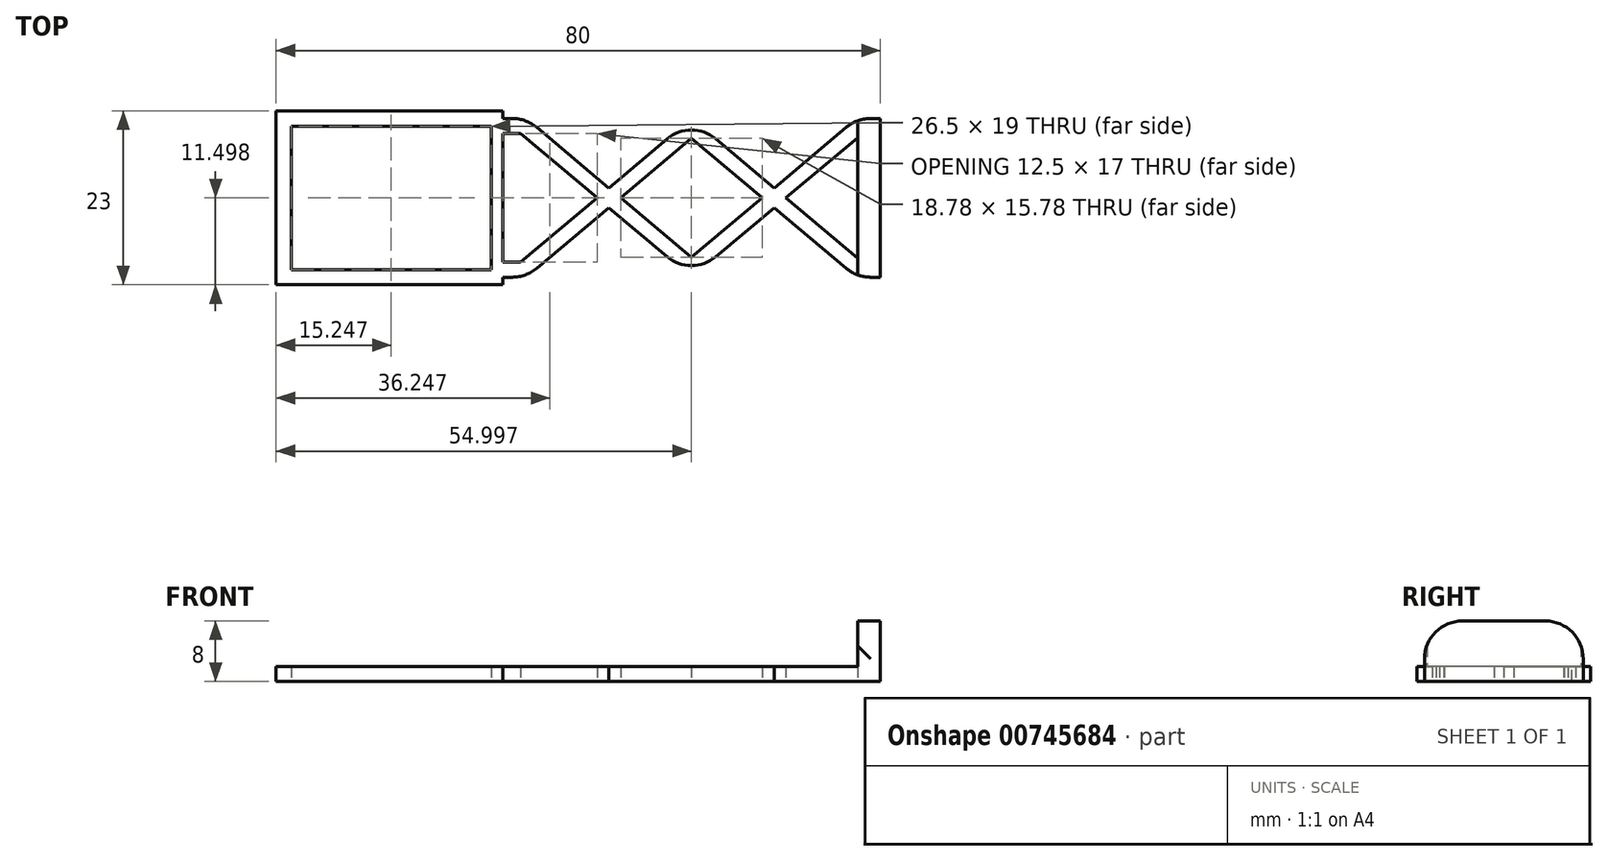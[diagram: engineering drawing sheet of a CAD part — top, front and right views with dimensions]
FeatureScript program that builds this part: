
annotation { "Feature Type Name" : "Feature", "Feature Type Description" : "" }
export const myFeature = defineFeature(function(context is Context, id is Id, definition is map)
    precondition{}
    {
        {
            var Q0;
            Q0=qCreatedBy(makeId("Top.planeOp"),FACE);
            var sketch = newSketch(context, id + "F0", { "sketchPlane" : qUnion([Q0])});
            skLineSegment(sketch, "E0.bottom", {"start": v(-35.23, 8.03) * mm, "end": v(-5.23, 8.03) * mm});
            skLineSegment(sketch, "E0.top", {"start": v(-35.23, -14.97) * mm, "end": v(-5.23, -14.97) * mm});
            skLineSegment(sketch, "E0.left", {"start": v(-35.23, 8.03) * mm, "end": v(-35.23, -14.97) * mm});
            skLineSegment(sketch, "E1.right", {"start": v(44.77, 7.03) * mm, "end": v(44.77, -13.97) * mm});
            skLineSegment(sketch, "E2", {"start": v(-5.23, 8.03) * mm, "end": v(-5.23, 7.03) * mm});
            skLineSegment(sketch, "E3", {"start": v(-5.23, -14.97) * mm, "end": v(-5.23, -13.97) * mm});
            skLineSegment(sketch, "E4.bottom", {"start": v(-33.23, 6.03) * mm, "end": v(-6.73, 6.03) * mm});
            skLineSegment(sketch, "E4.top", {"start": v(-33.23, -12.97) * mm, "end": v(-6.73, -12.97) * mm});
            skLineSegment(sketch, "E4.left", {"start": v(-33.23, 6.03) * mm, "end": v(-33.23, -12.97) * mm});
            skLineSegment(sketch, "E4.right", {"start": v(-6.73, 6.03) * mm, "end": v(-6.73, -12.97) * mm});
            skLineSegment(sketch, "E5", {"start": v(41.77, 7.03) * mm, "end": v(41.77, -13.97) * mm});
            skLineSegment(sketch, "E6", {"start": v(-5.23, 7.03) * mm, "end": v(-5.23, -13.97) * mm});
            skLineSegment(sketch, "E7", {"start": v(-5.23, 7.03) * mm, "end": v(44.77, 7.03) * mm});
            skLineSegment(sketch, "E8", {"start": v(-5.23, -13.97) * mm, "end": v(44.77, -13.97) * mm});
            skLineSegment(sketch, "E9", {"start": v(19.77, 7.03) * mm, "end": v(-5.23, -13.97) * mm});
            skLineSegment(sketch, "E10", {"start": v(19.77, 7.03) * mm, "end": v(44.77, -13.97) * mm});
            skLineSegment(sketch, "E11", {"start": v(-5.23, 7.03) * mm, "end": v(19.77, -13.97) * mm});
            skLineSegment(sketch, "E12", {"start": v(19.77, -13.97) * mm, "end": v(44.77, 7.03) * mm});
            skLineSegment(sketch, "E13", {"start": v(8.82, -4.78) * mm, "end": v(-2.12, -13.97) * mm});
            skLineSegment(sketch, "E14", {"start": v(8.82, -2.17) * mm, "end": v(-2.12, 7.03) * mm});
            skLineSegment(sketch, "E15", {"start": v(8.82, -4.78) * mm, "end": v(21.32, 5.72) * mm});
            skLineSegment(sketch, "E16", {"start": v(8.82, -2.17) * mm, "end": v(21.32, -12.67) * mm});
            skLineSegment(sketch, "E17", {"start": v(30.71, -4.78) * mm, "end": v(41.66, -13.97) * mm});
            skLineSegment(sketch, "E18", {"start": v(30.71, -2.17) * mm, "end": v(41.66, 7.03) * mm});
            skLineSegment(sketch, "E19", {"start": v(30.71, -2.17) * mm, "end": v(19.77, -11.36) * mm});
            skLineSegment(sketch, "E20", {"start": v(30.71, -4.78) * mm, "end": v(19.77, 4.42) * mm});
            skLineSegment(sketch, "E21", {"start": v(-5.23, 5.03) * mm, "end": v(0.26, 5.03) * mm});
            skLineSegment(sketch, "E22", {"start": v(-5.23, -11.97) * mm, "end": v(0.26, -11.97) * mm});
            skSolve(sketch);
        }
        {
            var Q0;
            Q0=makeQuery(id+"F0.imprint","IMPRINT",FACE,{"disambiguationData":[TD([[makeQuery(id+"F0.imprint","IMPRINT",EDGE,{"derivedFrom":sQuery(id+"F0.wireOp",EDGE,"E0.bottom")}),-1.0]])]});
            var Q1;
            {var subQ1=sQuery(id+"F0.wireOp",EDGE,"E6");var subQ3=sQuery(id+"F0.wireOp",EDGE,"E21");var subQ4=makeQuery(id+"F0.imprint","INTERSECT",VERTEX,{"derivedFrom":[subQ1,subQ3]});Q1=makeQuery(id+"F0.imprint","IMPRINT",FACE,{"disambiguationData":[TD([[makeQuery(id+"F0.imprint","IMPRINT",EDGE,{"disambiguationData":[TD([[subQ4,-1.0]])],"derivedFrom":subQ3}),1.0]])]});}
            var Q2;
            {var subQ1=sQuery(id+"F0.wireOp",EDGE,"E7");var subQ3=sQuery(id+"F0.wireOp",EDGE,"E14");var subQ4=makeQuery(id+"F0.imprint","INTERSECT",VERTEX,{"derivedFrom":[subQ1,subQ3]});Q2=makeQuery(id+"F0.imprint","IMPRINT",FACE,{"disambiguationData":[TD([[makeQuery(id+"F0.imprint","IMPRINT",EDGE,{"disambiguationData":[TD([[subQ4,1.0]])],"derivedFrom":subQ3}),1.0]])]});}
            var Q3;
            {var subQ1=sQuery(id+"F0.wireOp",EDGE,"E9");var subQ3=sQuery(id+"F0.wireOp",EDGE,"E11");var subQ4=makeQuery(id+"F0.imprint","INTERSECT",VERTEX,{"derivedFrom":[subQ1,subQ3]});Q3=makeQuery(id+"F0.imprint","IMPRINT",FACE,{"disambiguationData":[TD([[makeQuery(id+"F0.imprint","IMPRINT",EDGE,{"disambiguationData":[TD([[subQ4,1.0]])],"derivedFrom":subQ3}),1.0]])]});}
            var Q4;
            {var subQ1=sQuery(id+"F0.wireOp",EDGE,"E6");var subQ3=sQuery(id+"F0.wireOp",EDGE,"E22");var subQ4=makeQuery(id+"F0.imprint","INTERSECT",VERTEX,{"derivedFrom":[subQ1,subQ3]});Q4=makeQuery(id+"F0.imprint","IMPRINT",FACE,{"disambiguationData":[TD([[makeQuery(id+"F0.imprint","IMPRINT",EDGE,{"disambiguationData":[TD([[subQ4,-1.0]])],"derivedFrom":subQ3}),-1.0]])]});}
            var Q5;
            {var subQ1=sQuery(id+"F0.wireOp",EDGE,"E8");var subQ3=sQuery(id+"F0.wireOp",EDGE,"E13");var subQ4=makeQuery(id+"F0.imprint","INTERSECT",VERTEX,{"derivedFrom":[subQ1,subQ3]});Q5=makeQuery(id+"F0.imprint","IMPRINT",FACE,{"disambiguationData":[TD([[makeQuery(id+"F0.imprint","IMPRINT",EDGE,{"disambiguationData":[TD([[subQ4,1.0]])],"derivedFrom":subQ3}),-1.0]])]});}
            var Q6;
            {var subQ0=sQuery(id+"F0.wireOp",EDGE,"E11");var subQ1=sQuery(id+"F0.wireOp",EDGE,"E9");var subQ2=makeQuery(id+"F0.imprint","INTERSECT",VERTEX,{"derivedFrom":[subQ1,subQ0]});Q6=makeQuery(id+"F0.imprint","IMPRINT",FACE,{"disambiguationData":[TD([[makeQuery(id+"F0.imprint","IMPRINT",EDGE,{"disambiguationData":[TD([[subQ2,-1.0]])],"derivedFrom":subQ1}),1.0]])]});}
            var Q7;
            {var subQ1=sQuery(id+"F0.wireOp",EDGE,"E9");var subQ3=sQuery(id+"F0.wireOp",EDGE,"E11");var subQ4=makeQuery(id+"F0.imprint","INTERSECT",VERTEX,{"derivedFrom":[subQ1,subQ3]});Q7=makeQuery(id+"F0.imprint","IMPRINT",FACE,{"disambiguationData":[TD([[makeQuery(id+"F0.imprint","IMPRINT",EDGE,{"disambiguationData":[TD([[subQ4,1.0]])],"derivedFrom":subQ1}),1.0]])]});}
            var Q8;
            {var subQ0=sQuery(id+"F0.wireOp",EDGE,"E15");var subQ1=makeQuery(id+"F0.imprint","INTERSECT",VERTEX,{"derivedFrom":[subQ0,sQuery(id+"F0.wireOp",EDGE,"E20")]});Q8=makeQuery(id+"F0.imprint","IMPRINT",FACE,{"disambiguationData":[TD([[makeQuery(id+"F0.imprint","IMPRINT",EDGE,{"disambiguationData":[TD([[subQ1,1.0]])],"derivedFrom":subQ0}),1.0]])]});}
            var Q9;
            {var subQ0=sQuery(id+"F0.wireOp",EDGE,"E16");var subQ1=makeQuery(id+"F0.imprint","INTERSECT",VERTEX,{"derivedFrom":[subQ0,sQuery(id+"F0.wireOp",EDGE,"E19")]});Q9=makeQuery(id+"F0.imprint","IMPRINT",FACE,{"disambiguationData":[TD([[makeQuery(id+"F0.imprint","IMPRINT",EDGE,{"disambiguationData":[TD([[subQ1,1.0]])],"derivedFrom":subQ0}),-1.0]])]});}
            var Q10;
            {var subQ0=sQuery(id+"F0.wireOp",EDGE,"E16");var subQ1=sQuery(id+"F0.wireOp",EDGE,"E12");var subQ2=makeQuery(id+"F0.imprint","INTERSECT",VERTEX,{"derivedFrom":[subQ1,subQ0]});Q10=makeQuery(id+"F0.imprint","IMPRINT",FACE,{"disambiguationData":[TD([[makeQuery(id+"F0.imprint","IMPRINT",EDGE,{"disambiguationData":[TD([[subQ2,1.0]])],"derivedFrom":subQ0}),1.0]])]});}
            var Q11;
            {var subQ0=sQuery(id+"F0.wireOp",EDGE,"E15");var subQ1=sQuery(id+"F0.wireOp",EDGE,"E10");var subQ2=makeQuery(id+"F0.imprint","INTERSECT",VERTEX,{"derivedFrom":[subQ1,subQ0]});Q11=makeQuery(id+"F0.imprint","IMPRINT",FACE,{"disambiguationData":[TD([[makeQuery(id+"F0.imprint","IMPRINT",EDGE,{"disambiguationData":[TD([[subQ2,1.0]])],"derivedFrom":subQ0}),-1.0]])]});}
            var Q12;
            {var subQ1=sQuery(id+"F0.wireOp",EDGE,"E10");var subQ3=sQuery(id+"F0.wireOp",EDGE,"E12");var subQ4=makeQuery(id+"F0.imprint","INTERSECT",VERTEX,{"derivedFrom":[subQ1,subQ3]});Q12=makeQuery(id+"F0.imprint","IMPRINT",FACE,{"disambiguationData":[TD([[makeQuery(id+"F0.imprint","IMPRINT",EDGE,{"disambiguationData":[TD([[subQ4,1.0]])],"derivedFrom":subQ1}),-1.0]])]});}
            var Q13;
            {var subQ5=sQuery(id+"F0.wireOp",EDGE,"E18");Q13=makeQuery(id+"F0.imprint","IMPRINT",FACE,{"disambiguationData":[TD([[makeQuery(id+"F0.imprint","IMPRINT",EDGE,{"derivedFrom":subQ5}),-1.0]])]});}
            var Q14;
            {var subQ0=sQuery(id+"F0.wireOp",EDGE,"E17");Q14=makeQuery(id+"F0.imprint","IMPRINT",FACE,{"disambiguationData":[TD([[makeQuery(id+"F0.imprint","IMPRINT",EDGE,{"derivedFrom":subQ0}),1.0]])]});}
            extrude(context, id + "F1", {"entities" : qUnion([Q0, Q1, Q2, Q3, Q4, Q5, Q6, Q7, Q8, Q9, Q10, Q11, Q12, Q13, Q14]), "depth" : 2 * mm, "offsetDistance" : 25 * mm});
        }
        {
            var Q0;
            {var subQ0=sQuery(id+"F0.wireOp",EDGE,"E7");var subQ1=sQuery(id+"F0.wireOp",EDGE,"E5");var subQ2=makeQuery(id+"F0.imprint","INTERSECT",VERTEX,{"derivedFrom":[subQ1,subQ0]});Q0=makeQuery(id+"F0.imprint","IMPRINT",FACE,{"disambiguationData":[TD([[makeQuery(id+"F0.imprint","IMPRINT",EDGE,{"disambiguationData":[TD([[subQ2,-1.0]])],"derivedFrom":subQ1}),1.0]])]});}
            var Q1;
            {var subQ0=sQuery(id+"F0.wireOp",EDGE,"E1.right");Q1=makeQuery(id+"F0.imprint","IMPRINT",FACE,{"disambiguationData":[TD([[makeQuery(id+"F0.imprint","IMPRINT",EDGE,{"derivedFrom":subQ0}),-1.0]])]});}
            var Q2;
            {var subQ0=sQuery(id+"F0.wireOp",EDGE,"E8");var subQ1=sQuery(id+"F0.wireOp",EDGE,"E5");var subQ2=makeQuery(id+"F0.imprint","INTERSECT",VERTEX,{"derivedFrom":[subQ1,subQ0]});Q2=makeQuery(id+"F0.imprint","IMPRINT",FACE,{"disambiguationData":[TD([[makeQuery(id+"F0.imprint","IMPRINT",EDGE,{"disambiguationData":[TD([[subQ2,1.0]])],"derivedFrom":subQ1}),1.0]])]});}
            extrude(context, id + "F2", {"entities" : qUnion([Q0, Q1, Q2]), "operationType" : NewBodyOperationType.ADD, "depth" : 8 * mm, "offsetDistance" : 25 * mm});
        }
        {
            var Q0;
            Q0=makeQuery(id+"F1.opExtrude","SWEPT_EDGE",EDGE,{"disambiguationData":[OSD([sQuery(id+"F0.wireOp",EDGE,"E8"),sQuery(id+"F0.wireOp",EDGE,"E11"),sQuery(id+"F0.wireOp",EDGE,"E12")])]});
            var Q1;
            Q1=makeQuery(id+"F1.opExtrude","SWEPT_EDGE",EDGE,{"disambiguationData":[OSD([sQuery(id+"F0.wireOp",EDGE,"E7"),sQuery(id+"F0.wireOp",EDGE,"E9"),sQuery(id+"F0.wireOp",EDGE,"E10")])]});
            var Q2;
            Q2=makeQuery(id+"F1.opExtrude","SWEPT_EDGE",EDGE,{"disambiguationData":[OSD([sQuery(id+"F0.wireOp",EDGE,"E8"),sQuery(id+"F0.wireOp",EDGE,"E13")])]});
            var Q3;
            Q3=makeQuery(id+"F1.opExtrude","SWEPT_EDGE",EDGE,{"disambiguationData":[OSD([sQuery(id+"F0.wireOp",EDGE,"E7"),sQuery(id+"F0.wireOp",EDGE,"E14")])]});
            var Q4;
            Q4=makeQuery(id+"F1.opExtrude","SWEPT_EDGE",EDGE,{"disambiguationData":[OSD([sQuery(id+"F0.wireOp",EDGE,"E7"),sQuery(id+"F0.wireOp",EDGE,"E18")])]});
            var Q5;
            Q5=makeQuery(id+"F1.opExtrude","SWEPT_EDGE",EDGE,{"disambiguationData":[OSD([sQuery(id+"F0.wireOp",EDGE,"E8"),sQuery(id+"F0.wireOp",EDGE,"E17")])]});
            var Q6;
            Q6=makeQuery(id+"F2.opExtrude","CAP_EDGE",EDGE,{"disambiguationData":[OSD([sQuery(id+"F0.wireOp",EDGE,"E8")])],"isStart":false});
            var Q7;
            Q7=makeQuery(id+"F2.opExtrude","CAP_EDGE",EDGE,{"disambiguationData":[OSD([sQuery(id+"F0.wireOp",EDGE,"E7")])],"isStart":false});
            fillet(context, id + "F3", {"entities" : qUnion([Q0, Q1, Q2, Q3, Q4, Q5, Q6, Q7]), "tangentPropagation" : true, "radius" : 5 * mm, "defaultsChanged" : false, "vertexSettings" : [], "allowEdgeOverflow" : false});
        }
    });
